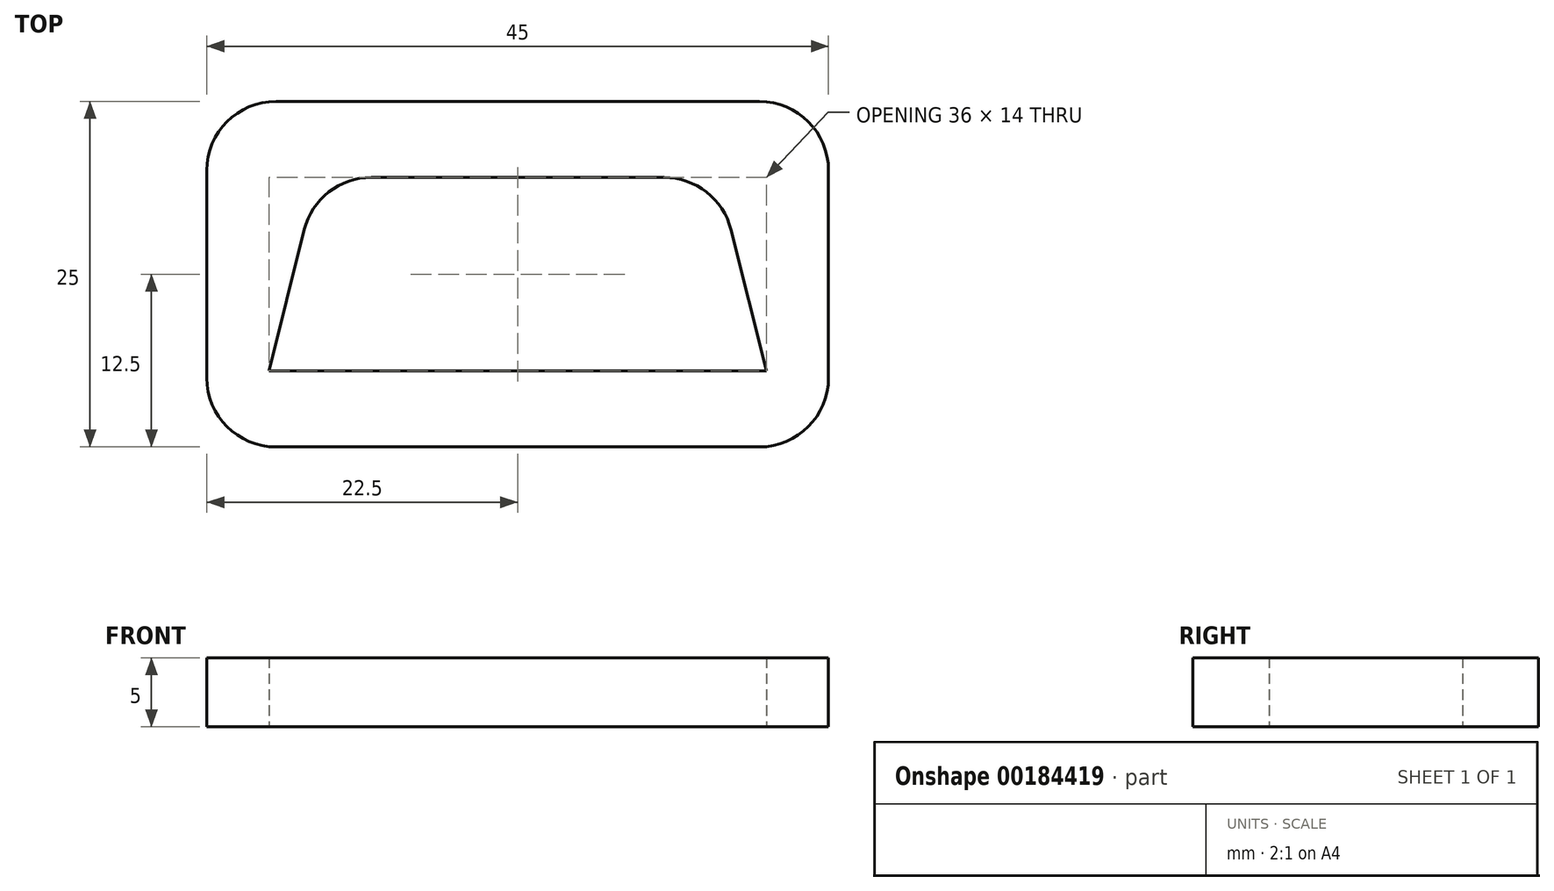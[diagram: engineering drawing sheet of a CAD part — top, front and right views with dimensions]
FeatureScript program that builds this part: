
annotation { "Feature Type Name" : "Feature", "Feature Type Description" : "" }
export const myFeature = defineFeature(function(context is Context, id is Id, definition is map)
    precondition{}
    {
        {
            var Q0;
            Q0=qCreatedBy(makeId("Top.planeOp"),FACE);
            var sketch = newSketch(context, id + "F0", { "sketchPlane" : qUnion([Q0])});
            skLineSegment(sketch, "E0", {"start": v(0, 0) * mm, "end": v(0, 14) * mm, "construction": true});
            skLineSegment(sketch, "E1", {"start": v(-18, 0) * mm, "end": v(18, 0) * mm});
            skLineSegment(sketch, "E2", {"start": v(18, 0) * mm, "end": v(14.5, 14) * mm});
            skLineSegment(sketch, "E3", {"start": v(14.5, 14) * mm, "end": v(-14.5, 14) * mm});
            skLineSegment(sketch, "E4", {"start": v(-14.5, 14) * mm, "end": v(-18, 0) * mm});
            skLineSegment(sketch, "E5.bottom", {"start": v(22.5, -5.5) * mm, "end": v(-22.5, -5.5) * mm});
            skLineSegment(sketch, "E5.top", {"start": v(22.5, 19.5) * mm, "end": v(-22.5, 19.5) * mm});
            skLineSegment(sketch, "E5.left", {"start": v(22.5, -5.5) * mm, "end": v(22.5, 19.5) * mm});
            skLineSegment(sketch, "E5.right", {"start": v(-22.5, -5.5) * mm, "end": v(-22.5, 19.5) * mm});
            skPoint(sketch, "E5.middle", {"position": v(0, 7) * mm});
            skSolve(sketch);
        }
        {
            var Q0;
            Q0=makeQuery(id+"F0.imprint","IMPRINT",FACE,{"disambiguationData":[TD([[makeQuery(id+"F0.imprint","IMPRINT",EDGE,{"derivedFrom":sQuery(id+"F0.wireOp",EDGE,"E1")}),-1.0]])]});
            extrude(context, id + "F1", {"entities" : qUnion([Q0]), "depth" : 5 * mm});
        }
        {
            var Q0;
            Q0=makeQuery(id+"F1.opExtrude","SWEPT_EDGE",EDGE,{"disambiguationData":[OSD([sQuery(id+"F0.wireOp",EDGE,"E5.top"),sQuery(id+"F0.wireOp",EDGE,"E5.right")])]});
            var Q1;
            Q1=makeQuery(id+"F1.opExtrude","SWEPT_EDGE",EDGE,{"disambiguationData":[OSD([sQuery(id+"F0.wireOp",EDGE,"E5.top"),sQuery(id+"F0.wireOp",EDGE,"E5.left")])]});
            var Q2;
            Q2=makeQuery(id+"F1.opExtrude","SWEPT_EDGE",EDGE,{"disambiguationData":[OSD([sQuery(id+"F0.wireOp",EDGE,"E5.bottom"),sQuery(id+"F0.wireOp",EDGE,"E5.right")])]});
            var Q3;
            Q3=makeQuery(id+"F1.opExtrude","SWEPT_EDGE",EDGE,{"disambiguationData":[OSD([sQuery(id+"F0.wireOp",EDGE,"E5.bottom"),sQuery(id+"F0.wireOp",EDGE,"E5.left")])]});
            var Q4;
            Q4=makeQuery(id+"F1.opExtrude","SWEPT_EDGE",EDGE,{"disambiguationData":[OSD([sQuery(id+"F0.wireOp",EDGE,"E3"),sQuery(id+"F0.wireOp",EDGE,"E4")])]});
            var Q5;
            Q5=makeQuery(id+"F1.opExtrude","SWEPT_EDGE",EDGE,{"disambiguationData":[OSD([sQuery(id+"F0.wireOp",EDGE,"E2"),sQuery(id+"F0.wireOp",EDGE,"E3")])]});
            fillet(context, id + "F2", {"entities" : qUnion([Q0, Q1, Q2, Q3, Q4, Q5]), "radius" : 5 * mm, "tangentPropagation" : true, "allowEdgeOverflow" : false});
        }
    });
